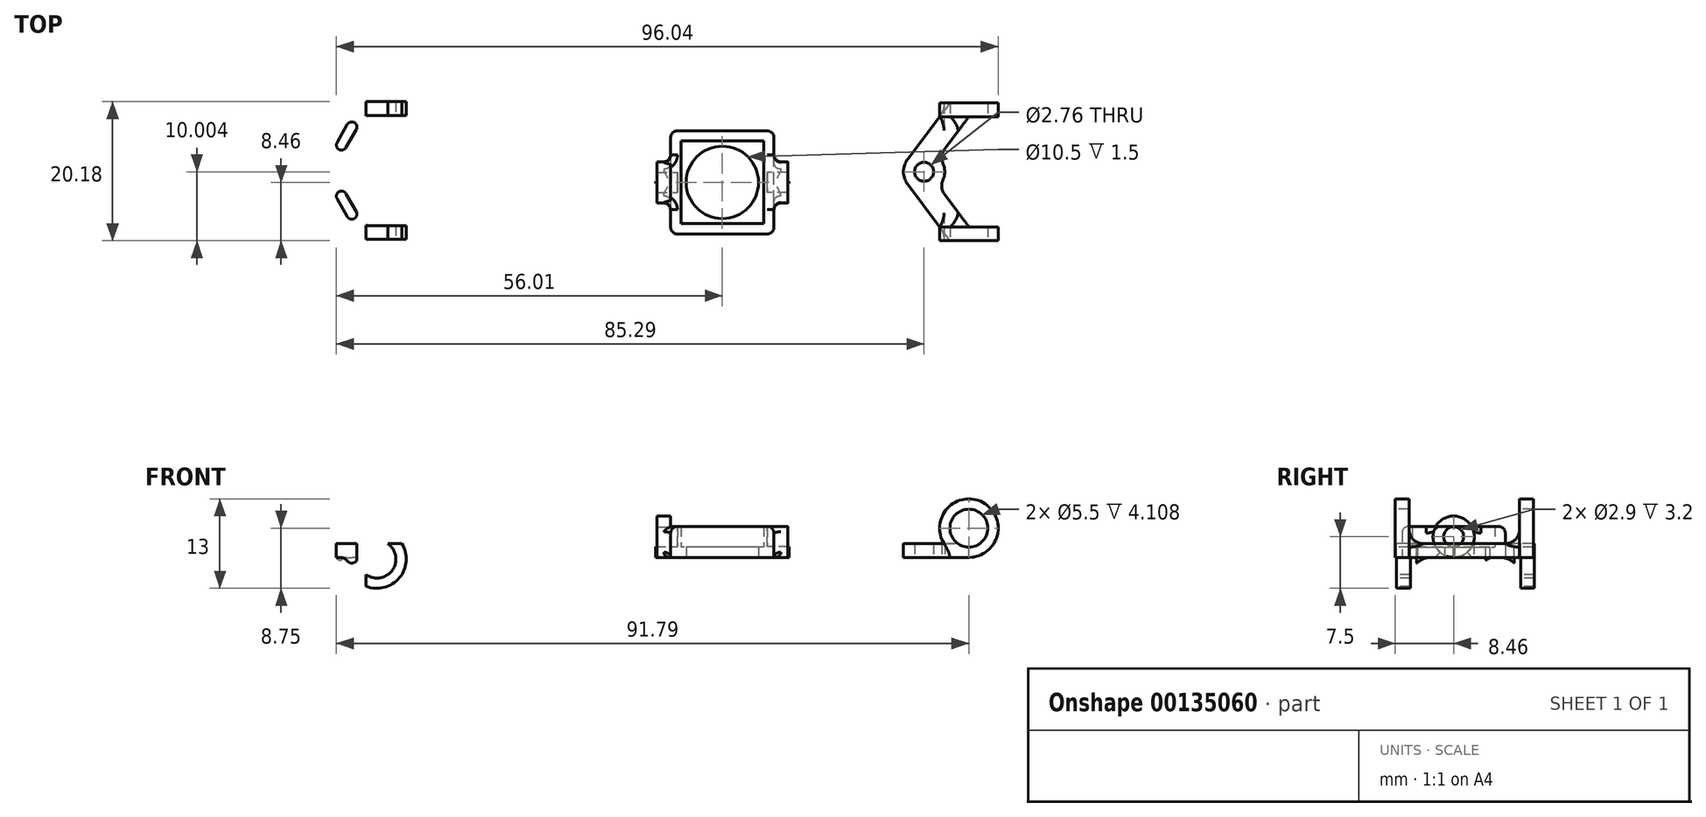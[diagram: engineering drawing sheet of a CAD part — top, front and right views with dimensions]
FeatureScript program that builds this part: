
annotation { "Feature Type Name" : "Feature", "Feature Type Description" : "" }
export const myFeature = defineFeature(function(context is Context, id is Id, definition is map)
    precondition{}
    {
        {
            var Q0;
            Q0=qCreatedBy(makeId("Top.planeOp"),FACE);
            var sketch = newSketch(context, id + "F0", { "sketchPlane" : qUnion([Q0])});
            skLineSegment(sketch, "E0.bottom", {"start": v(6, -6) * mm, "end": v(-6, -6) * mm});
            skLineSegment(sketch, "E0.top", {"start": v(6, 6) * mm, "end": v(-6, 6) * mm});
            skLineSegment(sketch, "E0.left", {"start": v(6, -6) * mm, "end": v(6, 6) * mm});
            skLineSegment(sketch, "E0.right", {"start": v(-6, -6) * mm, "end": v(-6, 6) * mm});
            skPoint(sketch, "E0.middle", {"position": v(0, 0) * mm});
            skLineSegment(sketch, "E1.bottom", {"start": v(7.5, -7.5) * mm, "end": v(-7.5, -7.5) * mm});
            skLineSegment(sketch, "E1.top", {"start": v(7.5, 7.5) * mm, "end": v(-7.5, 7.5) * mm});
            skLineSegment(sketch, "E1.left", {"start": v(7.5, -7.5) * mm, "end": v(7.5, 7.5) * mm});
            skLineSegment(sketch, "E1.right", {"start": v(-7.5, -7.5) * mm, "end": v(-7.5, 7.5) * mm});
            skCircle(sketch, "E2", {"center": v(0, 0) * mm, "radius": 5.25 * mm});
            skSolve(sketch);
        }
        {
            var Q0;
            Q0=makeQuery(id+"F0.imprint","IMPRINT",FACE,{"disambiguationData":[TD([[makeQuery(id+"F0.imprint","IMPRINT",EDGE,{"derivedFrom":sQuery(id+"F0.wireOp",EDGE,"E0.bottom")}),1.0]])]});
            extrude(context, id + "F1", {"entities" : qUnion([Q0]), "depth" : (3 + 1.5) * mm});
        }
        {
            var Q0;
            Q0=makeQuery(id+"F0.imprint","IMPRINT",FACE,{"disambiguationData":[TD([[makeQuery(id+"F0.imprint","IMPRINT",EDGE,{"derivedFrom":sQuery(id+"F0.wireOp",EDGE,"E0.bottom")}),-1.0]])]});
            extrude(context, id + "F2", {"entities" : qUnion([Q0]), "operationType" : NewBodyOperationType.ADD, "depth" : 1.5 * mm});
        }
        {
            var Q0;
            Q0=makeQuery(id+"F1.opExtrude","SWEPT_FACE",FACE,{"disambiguationData":[OSD([sQuery(id+"F0.wireOp",EDGE,"E1.right")])]});
            var sketch = newSketch(context, id + "F3", { "sketchPlane" : qUnion([Q0])});
            skLineSegment(sketch, "E3", {"start": v(0, 0) * mm, "end": v(0, 3) * mm, "construction": true});
            skPoint(sketch, "E3.endSnap0", {"position": v(0, 0) * mm});
            skCircle(sketch, "E4", {"center": v(0, 3) * mm, "radius": 3 * mm});
            skCircle(sketch, "E5", {"center": v(0, 3) * mm, "radius": 1.45 * mm});
            skSolve(sketch);
        }
        {
            var Q0;
            {var subQ0=sQuery(id+"F3.wireOp",EDGE,"E4");var subQ1=makeQuery(id+"F1.opExtrude","CAP_EDGE",EDGE,{"disambiguationData":[OSD([sQuery(id+"F0.wireOp",EDGE,"E1.right")])],"isStart":false});var subQ2=makeQuery(id+"F3.imprint","INTERSECT",VERTEX,{"disambiguationData":[OD(0.0)],"derivedFrom":[subQ1,subQ0]});Q0=makeQuery(id+"F3.imprint","IMPRINT",FACE,{"disambiguationData":[TD([[makeQuery(id+"F3.imprint","IMPRINT",EDGE,{"disambiguationData":[TD([[subQ2,1.0]])],"derivedFrom":subQ0}),1.0]])]});}
            var Q1;
            Q1=makeQuery(id+"F3.imprint","IMPRINT",FACE,{"disambiguationData":[TD([[makeQuery(id+"F3.imprint","IMPRINT",EDGE,{"derivedFrom":sQuery(id+"F3.wireOp",EDGE,"E5")}),-1.0]])]});
            extrude(context, id + "F4", {"entities" : qUnion([Q0, Q1]), "operationType" : NewBodyOperationType.ADD, "depth" : 2 * mm});
        }
        {
            var Q0;
            Q0=makeQuery(id+"F1.opExtrude","SWEPT_FACE",FACE,{"disambiguationData":[OSD([sQuery(id+"F0.wireOp",EDGE,"E1.left")])]});
            var sketch = newSketch(context, id + "F5", { "sketchPlane" : qUnion([Q0])});
            skLineSegment(sketch, "E6", {"start": v(0, 0) * mm, "end": v(0, 3) * mm, "construction": true});
            skPoint(sketch, "E6.endSnap0", {"position": v(0, 0) * mm});
            skCircle(sketch, "E7", {"center": v(0, 3) * mm, "radius": 3 * mm});
            skCircle(sketch, "E8", {"center": v(0, 3) * mm, "radius": 1.45 * mm});
            skSolve(sketch);
        }
        {
            var Q0;
            {var subQ0=sQuery(id+"F5.wireOp",EDGE,"E7");var subQ1=makeQuery(id+"F1.opExtrude","CAP_EDGE",EDGE,{"disambiguationData":[OSD([sQuery(id+"F0.wireOp",EDGE,"E1.left")])],"isStart":false});var subQ2=makeQuery(id+"F5.imprint","INTERSECT",VERTEX,{"disambiguationData":[OD(0.0)],"derivedFrom":[subQ1,subQ0]});Q0=makeQuery(id+"F5.imprint","IMPRINT",FACE,{"disambiguationData":[TD([[makeQuery(id+"F5.imprint","IMPRINT",EDGE,{"disambiguationData":[TD([[subQ2,1.0]])],"derivedFrom":subQ0}),1.0]])]});}
            var Q1;
            Q1=makeQuery(id+"F5.imprint","IMPRINT",FACE,{"disambiguationData":[TD([[makeQuery(id+"F5.imprint","IMPRINT",EDGE,{"derivedFrom":sQuery(id+"F5.wireOp",EDGE,"E8")}),-1.0]])]});
            extrude(context, id + "F6", {"entities" : qUnion([Q0, Q1]), "operationType" : NewBodyOperationType.ADD, "depth" : 2 * mm});
        }
        {
            var Q0;
            {var subQ0=sQuery(id+"F3.wireOp",EDGE,"E4");Q0=makeQuery(id+"F4.boolean.opBoolean","SPLIT",EDGE,{"disambiguationData":[topologyDisambiguationEdgeConnected([makeQuery(id+"F1.opExtrude","SWEPT_FACE",FACE,{"disambiguationData":[OSD([sQuery(id+"F0.wireOp",EDGE,"E1.right")])]}),makeQuery(id+"F4.opExtrude","SWEPT_FACE",FACE,{"disambiguationData":[OSD([subQ0])]})]),OD(0.0)],"derivedFrom":makeQuery(id+"F4.opExtrude","CAP_EDGE",EDGE,{"disambiguationData":[OSD([subQ0])],"isStart":true})});}
            var Q1;
            {var subQ0=sQuery(id+"F3.wireOp",EDGE,"E4");Q1=makeQuery(id+"F4.boolean.opBoolean","SPLIT",EDGE,{"disambiguationData":[topologyDisambiguationEdgeConnected([makeQuery(id+"F1.opExtrude","SWEPT_FACE",FACE,{"disambiguationData":[OSD([sQuery(id+"F0.wireOp",EDGE,"E1.right")])]}),makeQuery(id+"F4.opExtrude","SWEPT_FACE",FACE,{"disambiguationData":[OSD([subQ0])]})]),OD(1.0)],"derivedFrom":makeQuery(id+"F4.opExtrude","CAP_EDGE",EDGE,{"disambiguationData":[OSD([subQ0])],"isStart":true})});}
            var Q2;
            {var subQ0=sQuery(id+"F5.wireOp",EDGE,"E7");Q2=makeQuery(id+"F6.boolean.opBoolean","SPLIT",EDGE,{"disambiguationData":[topologyDisambiguationEdgeConnected([makeQuery(id+"F1.opExtrude","SWEPT_FACE",FACE,{"disambiguationData":[OSD([sQuery(id+"F0.wireOp",EDGE,"E1.left")])]}),makeQuery(id+"F6.opExtrude","SWEPT_FACE",FACE,{"disambiguationData":[OSD([subQ0])]})]),OD(0.0)],"derivedFrom":makeQuery(id+"F6.opExtrude","CAP_EDGE",EDGE,{"disambiguationData":[OSD([subQ0])],"isStart":true})});}
            var Q3;
            {var subQ0=sQuery(id+"F5.wireOp",EDGE,"E7");Q3=makeQuery(id+"F6.boolean.opBoolean","SPLIT",EDGE,{"disambiguationData":[topologyDisambiguationEdgeConnected([makeQuery(id+"F1.opExtrude","SWEPT_FACE",FACE,{"disambiguationData":[OSD([sQuery(id+"F0.wireOp",EDGE,"E1.left")])]}),makeQuery(id+"F6.opExtrude","SWEPT_FACE",FACE,{"disambiguationData":[OSD([subQ0])]})]),OD(1.0)],"derivedFrom":makeQuery(id+"F6.opExtrude","CAP_EDGE",EDGE,{"disambiguationData":[OSD([subQ0])],"isStart":true})});}
            fillet(context, id + "F7", {"entities" : qUnion([Q0, Q1, Q2, Q3]), "radius" : 1 * mm, "tangentPropagation" : true, "allowEdgeOverflow" : false});
        }
        {
            var Q0;
            {var subQ0=sQuery(id+"F0.wireOp",EDGE,"E1.right");Q0=makeQuery(id+"F4.boolean.opBoolean","SPLIT",EDGE,{"disambiguationData":[topologyDisambiguationEdgeConnected([makeQuery(id+"F1.opExtrude","CAP_FACE",FACE,{"disambiguationData":[OSD([sQuery(id+"F0.wireOp",EDGE,"E0.bottom"),sQuery(id+"F0.wireOp",EDGE,"E0.top"),sQuery(id+"F0.wireOp",EDGE,"E0.left"),sQuery(id+"F0.wireOp",EDGE,"E0.right"),sQuery(id+"F0.wireOp",EDGE,"E1.bottom"),sQuery(id+"F0.wireOp",EDGE,"E1.top"),sQuery(id+"F0.wireOp",EDGE,"E1.left"),subQ0])],"isStart":false}),makeQuery(id+"F4.opExtrude","CAP_FACE",FACE,{"disambiguationData":[OSD([sQuery(id+"F3.wireOp",EDGE,"E4"),sQuery(id+"F3.wireOp",EDGE,"E5")])],"isStart":true})])],"derivedFrom":makeQuery(id+"F1.opExtrude","CAP_EDGE",EDGE,{"disambiguationData":[OSD([subQ0])],"isStart":false})});}
            var Q1;
            {var subQ0=sQuery(id+"F0.wireOp",EDGE,"E1.left");Q1=makeQuery(id+"F6.boolean.opBoolean","SPLIT",EDGE,{"disambiguationData":[topologyDisambiguationEdgeConnected([makeQuery(id+"F1.opExtrude","CAP_FACE",FACE,{"disambiguationData":[OSD([sQuery(id+"F0.wireOp",EDGE,"E0.bottom"),sQuery(id+"F0.wireOp",EDGE,"E0.top"),sQuery(id+"F0.wireOp",EDGE,"E0.left"),sQuery(id+"F0.wireOp",EDGE,"E0.right"),sQuery(id+"F0.wireOp",EDGE,"E1.bottom"),sQuery(id+"F0.wireOp",EDGE,"E1.top"),subQ0,sQuery(id+"F0.wireOp",EDGE,"E1.right")])],"isStart":false}),makeQuery(id+"F6.opExtrude","CAP_FACE",FACE,{"disambiguationData":[OSD([sQuery(id+"F5.wireOp",EDGE,"E7"),sQuery(id+"F5.wireOp",EDGE,"E8")])],"isStart":true})])],"derivedFrom":makeQuery(id+"F1.opExtrude","CAP_EDGE",EDGE,{"disambiguationData":[OSD([subQ0])],"isStart":false})});}
            var Q2;
            {var subQ0=sQuery(id+"F3.wireOp",EDGE,"E4");var subQ1=sQuery(id+"F0.wireOp",EDGE,"E1.right");Q2=makeQuery(id+"F7.opFillet","TWEAK_EDGE",EDGE,{"derivedFrom":[makeQuery(id+"F4.boolean.opBoolean","TWEAK_VERTEX",VERTEX,{"disambiguationData":[OD(0.0)],"derivedFrom":[makeQuery(id+"F1.opExtrude","CAP_FACE",FACE,{"disambiguationData":[OSD([sQuery(id+"F0.wireOp",EDGE,"E0.bottom"),sQuery(id+"F0.wireOp",EDGE,"E0.top"),sQuery(id+"F0.wireOp",EDGE,"E0.left"),sQuery(id+"F0.wireOp",EDGE,"E0.right"),sQuery(id+"F0.wireOp",EDGE,"E1.bottom"),sQuery(id+"F0.wireOp",EDGE,"E1.top"),sQuery(id+"F0.wireOp",EDGE,"E1.left"),subQ1])],"isStart":false}),makeQuery(id+"F1.opExtrude","SWEPT_FACE",FACE,{"disambiguationData":[OSD([subQ1])]}),makeQuery(id+"F4.opExtrude","SWEPT_FACE",FACE,{"disambiguationData":[OSD([subQ0])]}),makeQuery(id+"F4.opExtrude","CAP_FACE",FACE,{"disambiguationData":[OSD([subQ0,sQuery(id+"F3.wireOp",EDGE,"E5")])],"isStart":true})]})]});}
            var Q3;
            {var subQ0=sQuery(id+"F3.wireOp",EDGE,"E4");var subQ1=sQuery(id+"F0.wireOp",EDGE,"E1.right");Q3=makeQuery(id+"F7.opFillet","TWEAK_EDGE",EDGE,{"derivedFrom":[makeQuery(id+"F4.boolean.opBoolean","TWEAK_VERTEX",VERTEX,{"disambiguationData":[OD(1.0)],"derivedFrom":[makeQuery(id+"F1.opExtrude","CAP_FACE",FACE,{"disambiguationData":[OSD([sQuery(id+"F0.wireOp",EDGE,"E0.bottom"),sQuery(id+"F0.wireOp",EDGE,"E0.top"),sQuery(id+"F0.wireOp",EDGE,"E0.left"),sQuery(id+"F0.wireOp",EDGE,"E0.right"),sQuery(id+"F0.wireOp",EDGE,"E1.bottom"),sQuery(id+"F0.wireOp",EDGE,"E1.top"),sQuery(id+"F0.wireOp",EDGE,"E1.left"),subQ1])],"isStart":false}),makeQuery(id+"F1.opExtrude","SWEPT_FACE",FACE,{"disambiguationData":[OSD([subQ1])]}),makeQuery(id+"F4.opExtrude","SWEPT_FACE",FACE,{"disambiguationData":[OSD([subQ0])]}),makeQuery(id+"F4.opExtrude","CAP_FACE",FACE,{"disambiguationData":[OSD([subQ0,sQuery(id+"F3.wireOp",EDGE,"E5")])],"isStart":true})]})]});}
            var Q4;
            {var subQ0=sQuery(id+"F5.wireOp",EDGE,"E7");var subQ1=sQuery(id+"F0.wireOp",EDGE,"E1.left");Q4=makeQuery(id+"F7.opFillet","TWEAK_EDGE",EDGE,{"derivedFrom":[makeQuery(id+"F6.boolean.opBoolean","TWEAK_VERTEX",VERTEX,{"disambiguationData":[OD(1.0)],"derivedFrom":[makeQuery(id+"F1.opExtrude","CAP_FACE",FACE,{"disambiguationData":[OSD([sQuery(id+"F0.wireOp",EDGE,"E0.bottom"),sQuery(id+"F0.wireOp",EDGE,"E0.top"),sQuery(id+"F0.wireOp",EDGE,"E0.left"),sQuery(id+"F0.wireOp",EDGE,"E0.right"),sQuery(id+"F0.wireOp",EDGE,"E1.bottom"),sQuery(id+"F0.wireOp",EDGE,"E1.top"),subQ1,sQuery(id+"F0.wireOp",EDGE,"E1.right")])],"isStart":false}),makeQuery(id+"F1.opExtrude","SWEPT_FACE",FACE,{"disambiguationData":[OSD([subQ1])]}),makeQuery(id+"F6.opExtrude","SWEPT_FACE",FACE,{"disambiguationData":[OSD([subQ0])]}),makeQuery(id+"F6.opExtrude","CAP_FACE",FACE,{"disambiguationData":[OSD([subQ0,sQuery(id+"F5.wireOp",EDGE,"E8")])],"isStart":true})]})]});}
            var Q5;
            {var subQ0=sQuery(id+"F5.wireOp",EDGE,"E7");var subQ1=sQuery(id+"F0.wireOp",EDGE,"E1.left");Q5=makeQuery(id+"F7.opFillet","TWEAK_EDGE",EDGE,{"derivedFrom":[makeQuery(id+"F6.boolean.opBoolean","TWEAK_VERTEX",VERTEX,{"disambiguationData":[OD(0.0)],"derivedFrom":[makeQuery(id+"F1.opExtrude","CAP_FACE",FACE,{"disambiguationData":[OSD([sQuery(id+"F0.wireOp",EDGE,"E0.bottom"),sQuery(id+"F0.wireOp",EDGE,"E0.top"),sQuery(id+"F0.wireOp",EDGE,"E0.left"),sQuery(id+"F0.wireOp",EDGE,"E0.right"),sQuery(id+"F0.wireOp",EDGE,"E1.bottom"),sQuery(id+"F0.wireOp",EDGE,"E1.top"),subQ1,sQuery(id+"F0.wireOp",EDGE,"E1.right")])],"isStart":false}),makeQuery(id+"F1.opExtrude","SWEPT_FACE",FACE,{"disambiguationData":[OSD([subQ1])]}),makeQuery(id+"F6.opExtrude","SWEPT_FACE",FACE,{"disambiguationData":[OSD([subQ0])]}),makeQuery(id+"F6.opExtrude","CAP_FACE",FACE,{"disambiguationData":[OSD([subQ0,sQuery(id+"F5.wireOp",EDGE,"E8")])],"isStart":true})]})]});}
            fillet(context, id + "F8", {"entities" : qUnion([Q0, Q1, Q2, Q3, Q4, Q5]), "radius" : 1 * mm, "tangentPropagation" : true, "allowEdgeOverflow" : false});
        }
        {
            var Q0;
            Q0=makeQuery(id+"F6.boolean.opBoolean","SPLIT",FACE,{"disambiguationData":[TD([makeQuery(id+"F6.opExtrude","SWEPT_FACE",FACE,{"disambiguationData":[OSD([sQuery(id+"F5.wireOp",EDGE,"E8")])]})])],"derivedFrom":makeQuery(id+"F1.opExtrude","SWEPT_FACE",FACE,{"disambiguationData":[OSD([sQuery(id+"F0.wireOp",EDGE,"E1.left")])]})});
            extrude(context, id + "F9", {"entities" : qUnion([Q0]), "operationType" : NewBodyOperationType.REMOVE, "oppositeDirection" : true, "depth" : 1 * mm});
        }
        {
            var Q0;
            Q0=makeQuery(id+"F4.boolean.opBoolean","SPLIT",FACE,{"disambiguationData":[TD([makeQuery(id+"F4.opExtrude","SWEPT_FACE",FACE,{"disambiguationData":[OSD([sQuery(id+"F3.wireOp",EDGE,"E5")])]})])],"derivedFrom":makeQuery(id+"F1.opExtrude","SWEPT_FACE",FACE,{"disambiguationData":[OSD([sQuery(id+"F0.wireOp",EDGE,"E1.right")])]})});
            extrude(context, id + "F10", {"entities" : qUnion([Q0]), "operationType" : NewBodyOperationType.REMOVE, "oppositeDirection" : true, "depth" : 1 * mm});
        }
        {
            var Q0;
            Q0=qCreatedBy(makeId("Top.planeOp"),FACE);
            var sketch = newSketch(context, id + "F11", { "sketchPlane" : qUnion([Q0])});
            skLineSegment(sketch, "E9", {"start": v(35.78, 11.54) * mm, "end": v(35.78, -8.46) * mm, "construction": true});
            skLineSegment(sketch, "E10", {"start": v(33.28, 1.54) * mm, "end": v(29.28, 1.54) * mm, "construction": true});
            skCircle(sketch, "E11", {"center": v(29.28, 1.54) * mm, "radius": 1.38 * mm});
            skCircle(sketch, "E12", {"center": v(29.28, 1.54) * mm, "radius": 3 * mm});
            skLineSegment(sketch, "E13", {"start": v(35.78, 1.54) * mm, "end": v(33.28, 1.54) * mm, "construction": true});
            skLineSegment(sketch, "E14.bottom", {"start": v(35.78, 11.54) * mm, "end": v(33.03, 11.54) * mm});
            skLineSegment(sketch, "E14.top", {"start": v(35.78, 9.54) * mm, "end": v(33.03, 9.54) * mm});
            skLineSegment(sketch, "E14.left", {"start": v(35.78, 11.54) * mm, "end": v(35.78, 9.54) * mm});
            skLineSegment(sketch, "E14.right", {"start": v(33.03, 11.54) * mm, "end": v(33.03, 9.54) * mm});
            skLineSegment(sketch, "E15.bottom", {"start": v(35.78, -8.46) * mm, "end": v(33.03, -8.46) * mm});
            skLineSegment(sketch, "E15.top", {"start": v(35.78, -6.46) * mm, "end": v(33.03, -6.46) * mm});
            skLineSegment(sketch, "E15.left", {"start": v(35.78, -8.46) * mm, "end": v(35.78, -6.46) * mm});
            skLineSegment(sketch, "E15.right", {"start": v(33.03, -8.46) * mm, "end": v(33.03, -6.46) * mm});
            skLineSegment(sketch, "E16", {"start": v(33.03, 11.54) * mm, "end": v(26.88, 3.34) * mm});
            skLineSegment(sketch, "E17", {"start": v(33.03, -8.46) * mm, "end": v(26.88, -0.26) * mm});
            skLineSegment(sketch, "E18", {"start": v(35.78, 9.54) * mm, "end": v(31.38, 3.68) * mm});
            skLineSegment(sketch, "E19", {"start": v(35.78, -6.46) * mm, "end": v(31.38, -0.6) * mm});
            skSolve(sketch);
        }
        {
            var Q0;
            Q0=makeQuery(id+"F11.imprint","IMPRINT",FACE,{"disambiguationData":[TD([[makeQuery(id+"F11.imprint","IMPRINT",EDGE,{"derivedFrom":sQuery(id+"F11.wireOp",EDGE,"E15.top")}),-1.0]])]});
            var Q1;
            Q1=makeQuery(id+"F11.imprint","IMPRINT",FACE,{"disambiguationData":[TD([[makeQuery(id+"F11.imprint","IMPRINT",EDGE,{"derivedFrom":sQuery(id+"F11.wireOp",EDGE,"E15.bottom")}),-1.0]])]});
            var Q2;
            Q2=makeQuery(id+"F11.imprint","IMPRINT",FACE,{"disambiguationData":[TD([[makeQuery(id+"F11.imprint","IMPRINT",EDGE,{"derivedFrom":sQuery(id+"F11.wireOp",EDGE,"E11")}),-1.0]])]});
            var Q3;
            Q3=makeQuery(id+"F11.imprint","IMPRINT",FACE,{"disambiguationData":[TD([[makeQuery(id+"F11.imprint","IMPRINT",EDGE,{"derivedFrom":sQuery(id+"F11.wireOp",EDGE,"E14.top")}),1.0]])]});
            var Q4;
            Q4=makeQuery(id+"F11.imprint","IMPRINT",FACE,{"disambiguationData":[TD([[makeQuery(id+"F11.imprint","IMPRINT",EDGE,{"derivedFrom":sQuery(id+"F11.wireOp",EDGE,"E14.bottom")}),1.0]])]});
            extrude(context, id + "F12", {"entities" : qUnion([Q0, Q1, Q2, Q3, Q4]), "depth" : 2 * mm});
        }
        {
            var Q0;
            Q0=makeQuery(id+"F12.opExtrude","SWEPT_FACE",FACE,{"disambiguationData":[OSD([sQuery(id+"F11.wireOp",EDGE,"E15.bottom")])]});
            var sketch = newSketch(context, id + "F13", { "sketchPlane" : qUnion([Q0])});
            skLineSegment(sketch, "E20", {"start": v(35.78, 0) * mm, "end": v(35.78, 4.25) * mm, "construction": true});
            skCircle(sketch, "E21", {"center": v(35.78, 4.25) * mm, "radius": 4.25 * mm});
            skCircle(sketch, "E22", {"center": v(35.78, 4.25) * mm, "radius": 2.75 * mm});
            skSolve(sketch);
        }
        {
            var Q0;
            {var subQ0=sQuery(id+"F11.wireOp",EDGE,"E15.bottom");var subQ1=makeQuery(id+"F12.opExtrude","CAP_EDGE",EDGE,{"disambiguationData":[OSD([subQ0])],"isStart":false});var subQ8=sQuery(id+"F13.wireOp",EDGE,"E22");var subQ10=makeQuery(id+"F13.imprint","INTERSECT",VERTEX,{"derivedFrom":[subQ1,subQ8]});Q0=makeQuery(id+"F13.imprint","IMPRINT",FACE,{"disambiguationData":[TD([[makeQuery(id+"F13.imprint","IMPRINT",EDGE,{"disambiguationData":[TD([[subQ10,1.0]])],"derivedFrom":subQ8}),-1.0]])]});}
            var Q1;
            {var subQ1=sQuery(id+"F11.wireOp",EDGE,"E15.bottom");var subQ4=sQuery(id+"F13.wireOp",EDGE,"E22");var subQ6=makeQuery(id+"F12.opExtrude","CAP_EDGE",EDGE,{"disambiguationData":[OSD([subQ1])],"isStart":false});var subQ7=makeQuery(id+"F13.imprint","INTERSECT",VERTEX,{"derivedFrom":[subQ6,subQ4]});Q1=makeQuery(id+"F13.imprint","IMPRINT",FACE,{"disambiguationData":[TD([[makeQuery(id+"F13.imprint","IMPRINT",EDGE,{"disambiguationData":[TD([[subQ7,-1.0]])],"derivedFrom":subQ4}),-1.0]])]});}
            extrude(context, id + "F14", {"entities" : qUnion([Q0, Q1]), "operationType" : NewBodyOperationType.ADD, "oppositeDirection" : true, "depth" : 2 * mm});
        }
        {
            var Q0;
            {var subQ0=sQuery(id+"F13.wireOp",EDGE,"E22");var subQ1=sQuery(id+"F11.wireOp",EDGE,"E15.bottom");var subQ4=makeQuery(id+"F12.opExtrude","CAP_EDGE",EDGE,{"disambiguationData":[OSD([subQ1])],"isStart":false});var subQ5=makeQuery(id+"F13.imprint","INTERSECT",VERTEX,{"derivedFrom":[subQ4,subQ0]});Q0=makeQuery(id+"F13.imprint","IMPRINT",FACE,{"disambiguationData":[TD([[makeQuery(id+"F13.imprint","IMPRINT",EDGE,{"disambiguationData":[TD([[subQ5,-1.0]])],"derivedFrom":subQ0}),1.0]])]});}
            extrude(context, id + "F15", {"entities" : qUnion([Q0]), "operationType" : NewBodyOperationType.REMOVE, "oppositeDirection" : true, "depth" : 25 * mm});
        }
        {
            var Q0;
            {var subQ0=sQuery(id+"F11.wireOp",EDGE,"E15.bottom");var subQ1=makeQuery(id+"F12.opExtrude","CAP_EDGE",EDGE,{"disambiguationData":[OSD([subQ0])],"isStart":false});var subQ8=sQuery(id+"F13.wireOp",EDGE,"E22");var subQ10=makeQuery(id+"F13.imprint","INTERSECT",VERTEX,{"derivedFrom":[subQ1,subQ8]});Q0=makeQuery(id+"F13.imprint","IMPRINT",FACE,{"disambiguationData":[TD([[makeQuery(id+"F13.imprint","IMPRINT",EDGE,{"disambiguationData":[TD([[subQ10,1.0]])],"derivedFrom":subQ8}),-1.0]])]});}
            var Q1;
            {var subQ1=sQuery(id+"F11.wireOp",EDGE,"E15.bottom");var subQ4=sQuery(id+"F13.wireOp",EDGE,"E22");var subQ6=makeQuery(id+"F12.opExtrude","CAP_EDGE",EDGE,{"disambiguationData":[OSD([subQ1])],"isStart":false});var subQ7=makeQuery(id+"F13.imprint","INTERSECT",VERTEX,{"derivedFrom":[subQ6,subQ4]});Q1=makeQuery(id+"F13.imprint","IMPRINT",FACE,{"disambiguationData":[TD([[makeQuery(id+"F13.imprint","IMPRINT",EDGE,{"disambiguationData":[TD([[subQ7,-1.0]])],"derivedFrom":subQ4}),-1.0]])]});}
            var Q2;
            Q2=makeQuery(id+"F12.opExtrude","SWEPT_FACE",FACE,{"disambiguationData":[OSD([sQuery(id+"F11.wireOp",EDGE,"E14.bottom")])]});
            extrude(context, id + "F16", {"entities" : qUnion([Q0, Q1]), "operationType" : NewBodyOperationType.ADD, "endBound" : BoundingType.UP_TO_SURFACE, "oppositeDirection" : true, "endBoundEntityFace" : qUnion([Q2]), "depth" : 25 * mm, "hasSecondDirection" : true, "secondDirectionOppositeDirection" : true, "secondDirectionDepth" : 18 * mm});
        }
        {
            var Q0;
            Q0=makeQuery(id+"F16.boolean.opBoolean","INTERSECT",EDGE,{"derivedFrom":[makeQuery(id+"F12.opExtrude","CAP_FACE",FACE,{"disambiguationData":[OSD([sQuery(id+"F11.wireOp",EDGE,"E11"),sQuery(id+"F11.wireOp",EDGE,"E12"),sQuery(id+"F11.wireOp",EDGE,"E14.bottom"),sQuery(id+"F11.wireOp",EDGE,"E14.left"),sQuery(id+"F11.wireOp",EDGE,"E15.bottom"),sQuery(id+"F11.wireOp",EDGE,"E15.left"),sQuery(id+"F11.wireOp",EDGE,"E16"),sQuery(id+"F11.wireOp",EDGE,"E17"),sQuery(id+"F11.wireOp",EDGE,"E18"),sQuery(id+"F11.wireOp",EDGE,"E19")])],"isStart":false}),makeQuery(id+"F16.opExtrude","CAP_FACE",FACE,{"disambiguationData":[OSD([sQuery(id+"F13.wireOp",EDGE,"E21"),sQuery(id+"F13.wireOp",EDGE,"E22")])],"isStart":true})]});
            var Q1;
            Q1=makeQuery(id+"F14.boolean.opBoolean","INTERSECT",EDGE,{"derivedFrom":[makeQuery(id+"F12.opExtrude","CAP_FACE",FACE,{"disambiguationData":[OSD([sQuery(id+"F11.wireOp",EDGE,"E11"),sQuery(id+"F11.wireOp",EDGE,"E12"),sQuery(id+"F11.wireOp",EDGE,"E14.bottom"),sQuery(id+"F11.wireOp",EDGE,"E14.left"),sQuery(id+"F11.wireOp",EDGE,"E15.bottom"),sQuery(id+"F11.wireOp",EDGE,"E15.left"),sQuery(id+"F11.wireOp",EDGE,"E16"),sQuery(id+"F11.wireOp",EDGE,"E17"),sQuery(id+"F11.wireOp",EDGE,"E18"),sQuery(id+"F11.wireOp",EDGE,"E19")])],"isStart":false}),makeQuery(id+"F14.opExtrude","CAP_FACE",FACE,{"disambiguationData":[OSD([sQuery(id+"F13.wireOp",EDGE,"E21"),sQuery(id+"F13.wireOp",EDGE,"E22")])],"isStart":false})]});
            var Q2;
            {var subQ0=sQuery(id+"F13.wireOp",EDGE,"E21");var subQ1=sQuery(id+"F11.wireOp",EDGE,"E19");var subQ2=sQuery(id+"F11.wireOp",EDGE,"E15.left");Q2=makeQuery(id+"F14.boolean.opBoolean","SPLIT",EDGE,{"disambiguationData":[TD([makeQuery(id+"F14.opExtrude","SWEPT_FACE",FACE,{"disambiguationData":[OSD([subQ0])]})])],"derivedFrom":makeQuery(id+"F12.opExtrude","SWEPT_EDGE",EDGE,{"disambiguationData":[OSD([sQuery(id+"F11.wireOp",EDGE,"E15.top"),subQ2,subQ1])]})});}
            var Q3;
            Q3=makeQuery(id+"F12.opExtrude","SWEPT_EDGE",EDGE,{"disambiguationData":[OSD([sQuery(id+"F11.wireOp",EDGE,"E14.top"),sQuery(id+"F11.wireOp",EDGE,"E14.left"),sQuery(id+"F11.wireOp",EDGE,"E18")])]});
            var Q4;
            Q4=makeQuery(id+"F12.opExtrude","SWEPT_EDGE",EDGE,{"disambiguationData":[OSD([sQuery(id+"F11.wireOp",EDGE,"E12"),sQuery(id+"F11.wireOp",EDGE,"E18")])]});
            var Q5;
            Q5=makeQuery(id+"F12.opExtrude","SWEPT_EDGE",EDGE,{"disambiguationData":[OSD([sQuery(id+"F11.wireOp",EDGE,"E12"),sQuery(id+"F11.wireOp",EDGE,"E19")])]});
            var Q6;
            Q6=makeQuery(id+"F14.boolean.opBoolean","INTERSECT",EDGE,{"derivedFrom":[makeQuery(id+"F12.opExtrude","SWEPT_FACE",FACE,{"disambiguationData":[OSD([sQuery(id+"F11.wireOp",EDGE,"E17")])]}),makeQuery(id+"F14.opExtrude","SWEPT_FACE",FACE,{"disambiguationData":[OSD([sQuery(id+"F13.wireOp",EDGE,"E21")])]})]});
            var Q7;
            Q7=makeQuery(id+"F16.boolean.opBoolean","INTERSECT",EDGE,{"derivedFrom":[makeQuery(id+"F12.opExtrude","SWEPT_FACE",FACE,{"disambiguationData":[OSD([sQuery(id+"F11.wireOp",EDGE,"E16")])]}),makeQuery(id+"F16.opExtrude","SWEPT_FACE",FACE,{"disambiguationData":[OSD([sQuery(id+"F13.wireOp",EDGE,"E21")])]})]});
            fillet(context, id + "F17", {"entities" : qUnion([Q0, Q1, Q2, Q3, Q4, Q5, Q6, Q7]), "radius" : 2 * mm, "tangentPropagation" : true, "allowEdgeOverflow" : false});
        }
        {
            var Q0;
            Q0=qCreatedBy(makeId("Top.planeOp"),FACE);
            var sketch = newSketch(context, id + "F18", { "sketchPlane" : qUnion([Q0])});
            skLineSegment(sketch, "E23", {"start": v(-50.12, 11.72) * mm, "end": v(-50.12, -8.28) * mm, "construction": true});
            skLineSegment(sketch, "E24", {"start": v(-50.12, 1.72) * mm, "end": v(-52.62, 1.72) * mm, "construction": true});
            skLineSegment(sketch, "E25", {"start": v(-52.62, 1.72) * mm, "end": v(-56.62, 1.72) * mm, "construction": true});
            skCircle(sketch, "E26", {"center": v(-56.62, 1.72) * mm, "radius": 1.45 * mm});
            skCircle(sketch, "E27", {"center": v(-56.62, 1.72) * mm, "radius": 3 * mm});
            skLineSegment(sketch, "E28.bottom", {"start": v(-50.12, 11.72) * mm, "end": v(-54.37, 11.72) * mm});
            skLineSegment(sketch, "E28.top", {"start": v(-50.12, 9.72) * mm, "end": v(-54.37, 9.72) * mm});
            skLineSegment(sketch, "E28.left", {"start": v(-50.12, 11.72) * mm, "end": v(-50.12, 9.72) * mm});
            skLineSegment(sketch, "E28.right", {"start": v(-54.37, 11.72) * mm, "end": v(-54.37, 9.72) * mm});
            skLineSegment(sketch, "E29.bottom", {"start": v(-50.12, -8.28) * mm, "end": v(-54.37, -8.28) * mm});
            skLineSegment(sketch, "E29.top", {"start": v(-50.12, -6.28) * mm, "end": v(-54.37, -6.28) * mm});
            skLineSegment(sketch, "E29.left", {"start": v(-50.12, -8.28) * mm, "end": v(-50.12, -6.28) * mm});
            skLineSegment(sketch, "E29.right", {"start": v(-54.37, -8.28) * mm, "end": v(-54.37, -6.28) * mm});
            skLineSegment(sketch, "E30", {"start": v(-54.37, 11.72) * mm, "end": v(-59.22, 3.2) * mm});
            skLineSegment(sketch, "E31", {"start": v(-54.37, -8.28) * mm, "end": v(-59.22, 0.23) * mm});
            skLineSegment(sketch, "E32", {"start": v(-50.12, -6.28) * mm, "end": v(-53.92, 0.4) * mm});
            skLineSegment(sketch, "E33", {"start": v(-50.12, 9.72) * mm, "end": v(-53.92, 3.04) * mm});
            skSolve(sketch);
        }
        {
            var Q0;
            Q0=makeQuery(id+"F18.imprint","IMPRINT",FACE,{"disambiguationData":[TD([[makeQuery(id+"F18.imprint","IMPRINT",EDGE,{"derivedFrom":sQuery(id+"F18.wireOp",EDGE,"E28.bottom")}),1.0]])]});
            var Q1;
            Q1=makeQuery(id+"F18.imprint","IMPRINT",FACE,{"disambiguationData":[TD([[makeQuery(id+"F18.imprint","IMPRINT",EDGE,{"derivedFrom":sQuery(id+"F18.wireOp",EDGE,"E28.top")}),1.0]])]});
            var Q2;
            Q2=makeQuery(id+"F18.imprint","IMPRINT",FACE,{"disambiguationData":[TD([[makeQuery(id+"F18.imprint","IMPRINT",EDGE,{"derivedFrom":sQuery(id+"F18.wireOp",EDGE,"E26")}),-1.0]])]});
            var Q3;
            Q3=makeQuery(id+"F18.imprint","IMPRINT",FACE,{"disambiguationData":[TD([[makeQuery(id+"F18.imprint","IMPRINT",EDGE,{"derivedFrom":sQuery(id+"F18.wireOp",EDGE,"E29.top")}),-1.0]])]});
            var Q4;
            Q4=makeQuery(id+"F18.imprint","IMPRINT",FACE,{"disambiguationData":[TD([[makeQuery(id+"F18.imprint","IMPRINT",EDGE,{"derivedFrom":sQuery(id+"F18.wireOp",EDGE,"E29.bottom")}),-1.0]])]});
            extrude(context, id + "F19", {"entities" : qUnion([Q0, Q1, Q2, Q3, Q4]), "depth" : 2 * mm});
        }
        {
            var Q0;
            Q0=makeQuery(id+"F19.opExtrude","SWEPT_FACE",FACE,{"disambiguationData":[OSD([sQuery(id+"F18.wireOp",EDGE,"E29.bottom")])]});
            var sketch = newSketch(context, id + "F20", { "sketchPlane" : qUnion([Q0])});
            skLineSegment(sketch, "E34", {"start": v(-50.12, 2) * mm, "end": v(-50.12, -0.25) * mm, "construction": true});
            skPoint(sketch, "E34.endSnap0", {"position": v(-50.12, 1) * mm});
            skCircle(sketch, "E35", {"center": v(-50.12, -0.25) * mm, "radius": 2.75 * mm});
            skCircle(sketch, "E36", {"center": v(-50.12, -0.25) * mm, "radius": 4.25 * mm});
            skLineSegment(sketch, "E37", {"start": v(-54.37, 2) * mm, "end": v(-46.51, 2) * mm});
            skSolve(sketch);
        }
        {
            var Q0;
            {var subQ0=sQuery(id+"F20.wireOp",EDGE,"E37");var subQ1=sQuery(id+"F20.wireOp",EDGE,"E35");var subQ2=makeQuery(id+"F20.imprint","INTERSECT",VERTEX,{"disambiguationData":[OD(0.0)],"derivedFrom":[subQ1,subQ0]});Q0=makeQuery(id+"F20.imprint","IMPRINT",FACE,{"disambiguationData":[TD([[makeQuery(id+"F20.imprint","IMPRINT",EDGE,{"disambiguationData":[TD([[subQ2,-1.0]])],"derivedFrom":subQ1}),-1.0]])]});}
            var Q1;
            {var subQ0=sQuery(id+"F20.wireOp",EDGE,"E37");var subQ1=sQuery(id+"F20.wireOp",EDGE,"E35");var subQ2=makeQuery(id+"F20.imprint","INTERSECT",VERTEX,{"disambiguationData":[OD(1.0)],"derivedFrom":[subQ1,subQ0]});Q1=makeQuery(id+"F20.imprint","IMPRINT",FACE,{"disambiguationData":[TD([[makeQuery(id+"F20.imprint","IMPRINT",EDGE,{"disambiguationData":[TD([[subQ2,1.0]])],"derivedFrom":subQ1}),-1.0]])]});}
            extrude(context, id + "F21", {"entities" : qUnion([Q0, Q1]), "operationType" : NewBodyOperationType.ADD, "oppositeDirection" : true, "depth" : 2 * mm});
        }
        {
            var Q0;
            {var subQ3=sQuery(id+"F18.wireOp",EDGE,"E29.bottom");var subQ6=makeQuery(id+"F19.opExtrude","SWEPT_EDGE",EDGE,{"disambiguationData":[OSD([subQ3,sQuery(id+"F18.wireOp",EDGE,"E29.left")])]});Q0=makeQuery(id+"F20.imprint","IMPRINT",FACE,{"disambiguationData":[TD([[makeQuery(id+"F20.imprint","IMPRINT",EDGE,{"derivedFrom":subQ6}),-1.0]])]});}
            extrude(context, id + "F22", {"entities" : qUnion([Q0]), "operationType" : NewBodyOperationType.REMOVE, "oppositeDirection" : true, "depth" : 25 * mm});
        }
        {
            var Q0;
            {var subQ0=sQuery(id+"F20.wireOp",EDGE,"E37");var subQ1=sQuery(id+"F20.wireOp",EDGE,"E35");var subQ2=makeQuery(id+"F20.imprint","INTERSECT",VERTEX,{"disambiguationData":[OD(0.0)],"derivedFrom":[subQ1,subQ0]});Q0=makeQuery(id+"F20.imprint","IMPRINT",FACE,{"disambiguationData":[TD([[makeQuery(id+"F20.imprint","IMPRINT",EDGE,{"disambiguationData":[TD([[subQ2,-1.0]])],"derivedFrom":subQ1}),-1.0]])]});}
            var Q1;
            {var subQ0=sQuery(id+"F20.wireOp",EDGE,"E37");var subQ1=sQuery(id+"F20.wireOp",EDGE,"E35");var subQ2=makeQuery(id+"F20.imprint","INTERSECT",VERTEX,{"disambiguationData":[OD(1.0)],"derivedFrom":[subQ1,subQ0]});Q1=makeQuery(id+"F20.imprint","IMPRINT",FACE,{"disambiguationData":[TD([[makeQuery(id+"F20.imprint","IMPRINT",EDGE,{"disambiguationData":[TD([[subQ2,1.0]])],"derivedFrom":subQ1}),-1.0]])]});}
            var Q2;
            Q2=makeQuery(id+"F19.opExtrude","SWEPT_FACE",FACE,{"disambiguationData":[OSD([sQuery(id+"F18.wireOp",EDGE,"E28.bottom")])]});
            extrude(context, id + "F23", {"entities" : qUnion([Q0, Q1]), "operationType" : NewBodyOperationType.ADD, "endBound" : BoundingType.UP_TO_SURFACE, "oppositeDirection" : true, "endBoundEntityFace" : qUnion([Q2]), "depth" : 25 * mm, "hasSecondDirection" : true, "secondDirectionOppositeDirection" : true, "secondDirectionDepth" : 18 * mm});
        }
        {
            var Q0;
            Q0=makeQuery(id+"F21.boolean.opBoolean","INTERSECT",EDGE,{"derivedFrom":[makeQuery(id+"F19.opExtrude","CAP_FACE",FACE,{"disambiguationData":[OSD([sQuery(id+"F18.wireOp",EDGE,"E26"),sQuery(id+"F18.wireOp",EDGE,"E27"),sQuery(id+"F18.wireOp",EDGE,"E28.bottom"),sQuery(id+"F18.wireOp",EDGE,"E28.left"),sQuery(id+"F18.wireOp",EDGE,"E29.bottom"),sQuery(id+"F18.wireOp",EDGE,"E29.left"),sQuery(id+"F18.wireOp",EDGE,"E30"),sQuery(id+"F18.wireOp",EDGE,"E31"),sQuery(id+"F18.wireOp",EDGE,"E32"),sQuery(id+"F18.wireOp",EDGE,"E33")])],"isStart":true}),makeQuery(id+"F21.opExtrude","CAP_FACE",FACE,{"disambiguationData":[OSD([sQuery(id+"F20.wireOp",EDGE,"E35"),sQuery(id+"F20.wireOp",EDGE,"E36"),sQuery(id+"F20.wireOp",EDGE,"E37")])],"isStart":false})]});
            var Q1;
            Q1=makeQuery(id+"F23.boolean.opBoolean","INTERSECT",EDGE,{"derivedFrom":[makeQuery(id+"F19.opExtrude","CAP_FACE",FACE,{"disambiguationData":[OSD([sQuery(id+"F18.wireOp",EDGE,"E26"),sQuery(id+"F18.wireOp",EDGE,"E27"),sQuery(id+"F18.wireOp",EDGE,"E28.bottom"),sQuery(id+"F18.wireOp",EDGE,"E28.left"),sQuery(id+"F18.wireOp",EDGE,"E29.bottom"),sQuery(id+"F18.wireOp",EDGE,"E29.left"),sQuery(id+"F18.wireOp",EDGE,"E30"),sQuery(id+"F18.wireOp",EDGE,"E31"),sQuery(id+"F18.wireOp",EDGE,"E32"),sQuery(id+"F18.wireOp",EDGE,"E33")])],"isStart":true}),makeQuery(id+"F23.opExtrude","CAP_FACE",FACE,{"disambiguationData":[OSD([sQuery(id+"F20.wireOp",EDGE,"E35"),sQuery(id+"F20.wireOp",EDGE,"E36"),sQuery(id+"F20.wireOp",EDGE,"E37")])],"isStart":true})]});
            var Q2;
            Q2=makeQuery(id+"F23.boolean.opBoolean","INTERSECT",EDGE,{"derivedFrom":[makeQuery(id+"F19.opExtrude","CAP_FACE",FACE,{"disambiguationData":[OSD([sQuery(id+"F18.wireOp",EDGE,"E26"),sQuery(id+"F18.wireOp",EDGE,"E27"),sQuery(id+"F18.wireOp",EDGE,"E28.bottom"),sQuery(id+"F18.wireOp",EDGE,"E28.left"),sQuery(id+"F18.wireOp",EDGE,"E29.bottom"),sQuery(id+"F18.wireOp",EDGE,"E29.left"),sQuery(id+"F18.wireOp",EDGE,"E30"),sQuery(id+"F18.wireOp",EDGE,"E31"),sQuery(id+"F18.wireOp",EDGE,"E32"),sQuery(id+"F18.wireOp",EDGE,"E33")])],"isStart":true}),makeQuery(id+"F23.opExtrude","SWEPT_FACE",FACE,{"disambiguationData":[OSD([sQuery(id+"F20.wireOp",EDGE,"E36")])]})]});
            var Q3;
            Q3=makeQuery(id+"F21.boolean.opBoolean","INTERSECT",EDGE,{"derivedFrom":[makeQuery(id+"F19.opExtrude","CAP_FACE",FACE,{"disambiguationData":[OSD([sQuery(id+"F18.wireOp",EDGE,"E26"),sQuery(id+"F18.wireOp",EDGE,"E27"),sQuery(id+"F18.wireOp",EDGE,"E28.bottom"),sQuery(id+"F18.wireOp",EDGE,"E28.left"),sQuery(id+"F18.wireOp",EDGE,"E29.bottom"),sQuery(id+"F18.wireOp",EDGE,"E29.left"),sQuery(id+"F18.wireOp",EDGE,"E30"),sQuery(id+"F18.wireOp",EDGE,"E31"),sQuery(id+"F18.wireOp",EDGE,"E32"),sQuery(id+"F18.wireOp",EDGE,"E33")])],"isStart":true}),makeQuery(id+"F21.opExtrude","SWEPT_FACE",FACE,{"disambiguationData":[OSD([sQuery(id+"F20.wireOp",EDGE,"E36")])]})]});
            fillet(context, id + "F24", {"entities" : qUnion([Q0, Q1, Q2, Q3]), "radius" : 3 * mm, "tangentPropagation" : true, "allowEdgeOverflow" : false});
        }
        {
            var Q0;
            Q0=makeQuery(id+"F19.opExtrude","CAP_FACE",FACE,{"disambiguationData":[OSD([sQuery(id+"F18.wireOp",EDGE,"E26"),sQuery(id+"F18.wireOp",EDGE,"E27"),sQuery(id+"F18.wireOp",EDGE,"E28.bottom"),sQuery(id+"F18.wireOp",EDGE,"E28.left"),sQuery(id+"F18.wireOp",EDGE,"E29.bottom"),sQuery(id+"F18.wireOp",EDGE,"E29.left"),sQuery(id+"F18.wireOp",EDGE,"E30"),sQuery(id+"F18.wireOp",EDGE,"E31"),sQuery(id+"F18.wireOp",EDGE,"E32"),sQuery(id+"F18.wireOp",EDGE,"E33")])],"isStart":true});
            var sketch = newSketch(context, id + "F25", { "sketchPlane" : qUnion([Q0])});
            skCircle(sketch, "E38", {"center": v(-56.62, -1.72) * mm, "radius": 3 * mm});
            skSolve(sketch);
        }
        {
            var Q0;
            Q0=makeQuery(id+"F25.imprint","IMPRINT",FACE,{"disambiguationData":[TD([[makeQuery(id+"F25.imprint","IMPRINT",EDGE,{"derivedFrom":makeQuery(id+"F19.opExtrude","CAP_EDGE",EDGE,{"disambiguationData":[OSD([sQuery(id+"F18.wireOp",EDGE,"E26")])],"isStart":true})}),1.0]])]});
            extrude(context, id + "F26", {"entities" : qUnion([Q0]), "operationType" : NewBodyOperationType.ADD, "depth" : 1.25 * mm});
        }
        {
            var Q0;
            {var subQ3=sQuery(id+"F18.wireOp",EDGE,"E30");var subQ4=sQuery(id+"F25.wireOp",EDGE,"E38");Q0=makeQuery(id+"F26.boolean.opBoolean","SPLIT",EDGE,{"disambiguationData":[TD([makeQuery(id+"F19.opExtrude","SWEPT_FACE",FACE,{"disambiguationData":[OSD([subQ3])]})])],"derivedFrom":makeQuery(id+"F26.opExtrude","CAP_EDGE",EDGE,{"disambiguationData":[OSD([subQ4])],"isStart":true})});}
            var Q1;
            {var subQ0=sQuery(id+"F18.wireOp",EDGE,"E31");var subQ5=sQuery(id+"F25.wireOp",EDGE,"E38");Q1=makeQuery(id+"F26.boolean.opBoolean","SPLIT",EDGE,{"disambiguationData":[TD([makeQuery(id+"F19.opExtrude","SWEPT_FACE",FACE,{"disambiguationData":[OSD([subQ0])]})])],"derivedFrom":makeQuery(id+"F26.opExtrude","CAP_EDGE",EDGE,{"disambiguationData":[OSD([subQ5])],"isStart":true})});}
            fillet(context, id + "F27", {"entities" : qUnion([Q0, Q1]), "radius" : 1 * mm, "tangentPropagation" : true, "allowEdgeOverflow" : false});
        }
        {
            var Q0;
            Q0=makeQuery(id+"F19.opExtrude","SWEPT_EDGE",EDGE,{"disambiguationData":[OSD([sQuery(id+"F18.wireOp",EDGE,"E27"),sQuery(id+"F18.wireOp",EDGE,"E33")])]});
            var Q1;
            Q1=makeQuery(id+"F19.opExtrude","SWEPT_EDGE",EDGE,{"disambiguationData":[OSD([sQuery(id+"F18.wireOp",EDGE,"E27"),sQuery(id+"F18.wireOp",EDGE,"E32")])]});
            fillet(context, id + "F28", {"entities" : qUnion([Q0, Q1]), "radius" : 1 * mm, "tangentPropagation" : true, "allowEdgeOverflow" : false});
        }
        {
            var Q0;
            Q0=makeQuery(id+"F19.opExtrude","CAP_FACE",FACE,{"disambiguationData":[OSD([sQuery(id+"F18.wireOp",EDGE,"E26"),sQuery(id+"F18.wireOp",EDGE,"E27"),sQuery(id+"F18.wireOp",EDGE,"E28.bottom"),sQuery(id+"F18.wireOp",EDGE,"E28.left"),sQuery(id+"F18.wireOp",EDGE,"E29.bottom"),sQuery(id+"F18.wireOp",EDGE,"E29.left"),sQuery(id+"F18.wireOp",EDGE,"E30"),sQuery(id+"F18.wireOp",EDGE,"E31"),sQuery(id+"F18.wireOp",EDGE,"E32"),sQuery(id+"F18.wireOp",EDGE,"E33")])],"isStart":false});
            var sketch = newSketch(context, id + "F29", { "sketchPlane" : qUnion([Q0])});
            skLineSegment(sketch, "E39", {"start": v(-56.8, 7.46) * mm, "end": v(-52.73, 5.14) * mm, "construction": true});
            skLineSegment(sketch, "E40", {"start": v(-56.8, -4.02) * mm, "end": v(-52.73, -1.7) * mm, "construction": true});
            skLineSegment(sketch, "E41", {"start": v(-54.76, 6.3) * mm, "end": v(-55.26, 5.43) * mm, "construction": true});
            skLineSegment(sketch, "E42", {"start": v(-55.26, 5.43) * mm, "end": v(-53.77, 8.04) * mm});
            skArc(sketch, "E43.0.startCap", {"start": v(-54.6, 5.06) * mm, "mid": v(-55.63, 4.78) * mm, "end": v(-55.9, 5.8) * mm});
            skArc(sketch, "E43.0.endCap", {"start": v(-54.42, 8.41) * mm, "mid": v(-53.4, 8.7) * mm, "end": v(-53.12, 7.67) * mm});
            skLineSegment(sketch, "E43.0.left", {"start": v(-55.9, 5.8) * mm, "end": v(-54.42, 8.41) * mm});
            skLineSegment(sketch, "E43.0.right", {"start": v(-54.6, 5.06) * mm, "end": v(-53.12, 7.67) * mm});
            skLineSegment(sketch, "E44", {"start": v(-54.76, -2.86) * mm, "end": v(-55.26, -2) * mm, "construction": true});
            skLineSegment(sketch, "E45", {"start": v(-55.26, -2) * mm, "end": v(-53.77, -4.6) * mm});
            skArc(sketch, "E46.0.startCap", {"start": v(-55.9, -2.37) * mm, "mid": v(-55.63, -1.34) * mm, "end": v(-54.6, -1.62) * mm});
            skArc(sketch, "E46.0.endCap", {"start": v(-53.12, -4.23) * mm, "mid": v(-53.4, -5.25) * mm, "end": v(-54.42, -4.97) * mm});
            skLineSegment(sketch, "E46.0.left", {"start": v(-54.6, -1.62) * mm, "end": v(-53.12, -4.23) * mm});
            skLineSegment(sketch, "E46.0.right", {"start": v(-55.9, -2.37) * mm, "end": v(-54.42, -4.97) * mm});
            skSolve(sketch);
        }
        {
            var Q0;
            Q0=makeQuery(id+"F29.imprint","IMPRINT",FACE,{"disambiguationData":[TD([[makeQuery(id+"F29.imprint","IMPRINT",EDGE,{"derivedFrom":sQuery(id+"F29.wireOp",EDGE,"E43.0.startCap")}),-1.0]])]});
            var Q1;
            Q1=makeQuery(id+"F29.imprint","IMPRINT",FACE,{"disambiguationData":[TD([[makeQuery(id+"F29.imprint","IMPRINT",EDGE,{"derivedFrom":sQuery(id+"F29.wireOp",EDGE,"E46.0.startCap")}),-1.0]])]});
            extrude(context, id + "F30", {"entities" : qUnion([Q0, Q1]), "operationType" : NewBodyOperationType.REMOVE, "oppositeDirection" : true, "depth" : 25 * mm});
        }
        {
            var Q0;
            Q0=makeQuery(id+"F1.opExtrude","SWEPT_EDGE",EDGE,{"disambiguationData":[OSD([sQuery(id+"F0.wireOp",EDGE,"E1.top"),sQuery(id+"F0.wireOp",EDGE,"E1.right")])]});
            var Q1;
            Q1=makeQuery(id+"F1.opExtrude","SWEPT_EDGE",EDGE,{"disambiguationData":[OSD([sQuery(id+"F0.wireOp",EDGE,"E1.bottom"),sQuery(id+"F0.wireOp",EDGE,"E1.right")])]});
            var Q2;
            Q2=makeQuery(id+"F1.opExtrude","SWEPT_EDGE",EDGE,{"disambiguationData":[OSD([sQuery(id+"F0.wireOp",EDGE,"E1.bottom"),sQuery(id+"F0.wireOp",EDGE,"E1.left")])]});
            var Q3;
            Q3=makeQuery(id+"F1.opExtrude","SWEPT_EDGE",EDGE,{"disambiguationData":[OSD([sQuery(id+"F0.wireOp",EDGE,"E1.top"),sQuery(id+"F0.wireOp",EDGE,"E1.left")])]});
            fillet(context, id + "F31", {"entities" : qUnion([Q0, Q1, Q2, Q3]), "radius" : 1 * mm, "tangentPropagation" : true, "allowEdgeOverflow" : false});
        }
        {
            var Q0;
            Q0=makeQuery(id+"F4.opExtrude","CAP_FACE",FACE,{"disambiguationData":[OSD([sQuery(id+"F3.wireOp",EDGE,"E4"),sQuery(id+"F3.wireOp",EDGE,"E5")])],"isStart":false});
            var sketch = newSketch(context, id + "F32", { "sketchPlane" : qUnion([Q0])});
            skLineSegment(sketch, "E47", {"start": v(0, 3) * mm, "end": v(0, 0) * mm});
            skArc(sketch, "E48.0.startCap", {"start": v(-0.1, 3) * mm, "mid": v(0, 3.1) * mm, "end": v(0.1, 3) * mm});
            skArc(sketch, "E48.0.endCap", {"start": v(0.1, 0) * mm, "mid": v(0, -0.1) * mm, "end": v(-0.1, 0) * mm});
            skLineSegment(sketch, "E48.0.left", {"start": v(0.1, 3) * mm, "end": v(0.1, 0) * mm});
            skLineSegment(sketch, "E48.0.right", {"start": v(-0.1, 3) * mm, "end": v(-0.1, 0) * mm});
            skSolve(sketch);
        }
        {
            var Q0;
            {var subQ0=sQuery(id+"F32.wireOp",EDGE,"E47");var subQ1=makeQuery(id+"F4.opExtrude","CAP_EDGE",EDGE,{"disambiguationData":[OSD([sQuery(id+"F3.wireOp",EDGE,"E4")])],"isStart":false});var subQ2=makeQuery(id+"F32.imprint","INTERSECT",VERTEX,{"derivedFrom":[subQ1,subQ0]});Q0=makeQuery(id+"F32.imprint","IMPRINT",FACE,{"disambiguationData":[TD([[makeQuery(id+"F32.imprint","IMPRINT",EDGE,{"disambiguationData":[TD([[subQ2,1.0]])],"derivedFrom":subQ0}),-1.0]])]});}
            var Q1;
            {var subQ0=sQuery(id+"F32.wireOp",EDGE,"E47");var subQ1=makeQuery(id+"F4.opExtrude","CAP_EDGE",EDGE,{"disambiguationData":[OSD([sQuery(id+"F3.wireOp",EDGE,"E4")])],"isStart":false});var subQ2=makeQuery(id+"F32.imprint","INTERSECT",VERTEX,{"derivedFrom":[subQ1,subQ0]});Q1=makeQuery(id+"F32.imprint","IMPRINT",FACE,{"disambiguationData":[TD([[makeQuery(id+"F32.imprint","IMPRINT",EDGE,{"disambiguationData":[TD([[subQ2,1.0]])],"derivedFrom":subQ0}),1.0]])]});}
            extrude(context, id + "F33", {"entities" : qUnion([Q0, Q1]), "operationType" : NewBodyOperationType.ADD, "depth" : 0.2 * mm});
        }
        {
            var Q0;
            Q0=makeQuery(id+"F6.opExtrude","CAP_FACE",FACE,{"disambiguationData":[OSD([sQuery(id+"F5.wireOp",EDGE,"E7"),sQuery(id+"F5.wireOp",EDGE,"E8")])],"isStart":false});
            var sketch = newSketch(context, id + "F34", { "sketchPlane" : qUnion([Q0])});
            skLineSegment(sketch, "E49", {"start": v(0, 3) * mm, "end": v(0, 0) * mm});
            skArc(sketch, "E50.0.startCap", {"start": v(-0.1, 3) * mm, "mid": v(0, 3.1) * mm, "end": v(0.1, 3) * mm});
            skArc(sketch, "E50.0.endCap", {"start": v(0.1, 0) * mm, "mid": v(0, -0.1) * mm, "end": v(-0.1, 0) * mm});
            skLineSegment(sketch, "E50.0.left", {"start": v(0.1, 3) * mm, "end": v(0.1, 0) * mm});
            skLineSegment(sketch, "E50.0.right", {"start": v(-0.1, 3) * mm, "end": v(-0.1, 0) * mm});
            skSolve(sketch);
        }
        {
            var Q0;
            {var subQ0=sQuery(id+"F34.wireOp",EDGE,"E49");var subQ1=makeQuery(id+"F6.opExtrude","CAP_EDGE",EDGE,{"disambiguationData":[OSD([sQuery(id+"F5.wireOp",EDGE,"E7")])],"isStart":false});var subQ2=makeQuery(id+"F34.imprint","INTERSECT",VERTEX,{"derivedFrom":[subQ1,subQ0]});Q0=makeQuery(id+"F34.imprint","IMPRINT",FACE,{"disambiguationData":[TD([[makeQuery(id+"F34.imprint","IMPRINT",EDGE,{"disambiguationData":[TD([[subQ2,1.0]])],"derivedFrom":subQ0}),-1.0]])]});}
            var Q1;
            {var subQ0=sQuery(id+"F34.wireOp",EDGE,"E49");var subQ1=makeQuery(id+"F6.opExtrude","CAP_EDGE",EDGE,{"disambiguationData":[OSD([sQuery(id+"F5.wireOp",EDGE,"E7")])],"isStart":false});var subQ2=makeQuery(id+"F34.imprint","INTERSECT",VERTEX,{"derivedFrom":[subQ1,subQ0]});Q1=makeQuery(id+"F34.imprint","IMPRINT",FACE,{"disambiguationData":[TD([[makeQuery(id+"F34.imprint","IMPRINT",EDGE,{"disambiguationData":[TD([[subQ2,1.0]])],"derivedFrom":subQ0}),1.0]])]});}
            extrude(context, id + "F35", {"entities" : qUnion([Q0, Q1]), "operationType" : NewBodyOperationType.ADD, "depth" : 0.2 * mm});
        }
        {
            var Q0;
            Q0=makeQuery(id+"F19.opExtrude","CAP_FACE",FACE,{"disambiguationData":[OSD([sQuery(id+"F18.wireOp",EDGE,"E26"),sQuery(id+"F18.wireOp",EDGE,"E27"),sQuery(id+"F18.wireOp",EDGE,"E28.bottom"),sQuery(id+"F18.wireOp",EDGE,"E28.left"),sQuery(id+"F18.wireOp",EDGE,"E29.bottom"),sQuery(id+"F18.wireOp",EDGE,"E29.left"),sQuery(id+"F18.wireOp",EDGE,"E30"),sQuery(id+"F18.wireOp",EDGE,"E31"),sQuery(id+"F18.wireOp",EDGE,"E32"),sQuery(id+"F18.wireOp",EDGE,"E33")])],"isStart":false});
            var sketch = newSketch(context, id + "F36", { "sketchPlane" : qUnion([Q0])});
            skLineSegment(sketch, "E51", {"start": v(-56.62, 1.72) * mm, "end": v(-53.62, 1.72) * mm, "construction": true});
            skLineSegment(sketch, "E52.1.0", {"start": v(-56.62, 1.72) * mm, "end": v(-53.66, 2.24) * mm, "construction": true});
            skLineSegment(sketch, "E52.2.0", {"start": v(-56.62, 1.72) * mm, "end": v(-53.8, 2.75) * mm, "construction": true});
            skLineSegment(sketch, "E52.3.0", {"start": v(-56.62, 1.72) * mm, "end": v(-54.02, 3.22) * mm, "construction": true});
            skLineSegment(sketch, "E52.4.0", {"start": v(-56.62, 1.72) * mm, "end": v(-54.32, 3.65) * mm, "construction": true});
            skLineSegment(sketch, "E52.5.0", {"start": v(-56.62, 1.72) * mm, "end": v(-54.69, 4.02) * mm, "construction": true});
            skLineSegment(sketch, "E52.6.0", {"start": v(-56.62, 1.72) * mm, "end": v(-55.12, 4.32) * mm, "construction": true});
            skLineSegment(sketch, "E52.7.0", {"start": v(-56.62, 1.72) * mm, "end": v(-55.6, 4.54) * mm, "construction": true});
            skLineSegment(sketch, "E52.8.0", {"start": v(-56.62, 1.72) * mm, "end": v(-56.1, 4.67) * mm, "construction": true});
            skLineSegment(sketch, "E52.9.0", {"start": v(-56.62, 1.72) * mm, "end": v(-56.62, 4.72) * mm, "construction": true});
            skLineSegment(sketch, "E52.10.0", {"start": v(-56.62, 1.72) * mm, "end": v(-57.14, 4.67) * mm, "construction": true});
            skLineSegment(sketch, "E52.11.0", {"start": v(-56.62, 1.72) * mm, "end": v(-57.64, 4.54) * mm, "construction": true});
            skLineSegment(sketch, "E52.12.0", {"start": v(-56.62, 1.72) * mm, "end": v(-58.12, 4.32) * mm, "construction": true});
            skLineSegment(sketch, "E52.13.0", {"start": v(-56.62, 1.72) * mm, "end": v(-58.54, 4.02) * mm, "construction": true});
            skLineSegment(sketch, "E52.14.0", {"start": v(-56.62, 1.72) * mm, "end": v(-58.91, 3.65) * mm, "construction": true});
            skLineSegment(sketch, "E52.15.0", {"start": v(-56.62, 1.72) * mm, "end": v(-59.21, 3.22) * mm, "construction": true});
            skLineSegment(sketch, "E52.16.0", {"start": v(-56.62, 1.72) * mm, "end": v(-59.44, 2.75) * mm, "construction": true});
            skLineSegment(sketch, "E52.17.0", {"start": v(-56.62, 1.72) * mm, "end": v(-59.57, 2.24) * mm, "construction": true});
            skLineSegment(sketch, "E52.18.0", {"start": v(-56.62, 1.72) * mm, "end": v(-59.62, 1.72) * mm, "construction": true});
            skLineSegment(sketch, "E52.19.0", {"start": v(-56.62, 1.72) * mm, "end": v(-59.57, 1.2) * mm, "construction": true});
            skLineSegment(sketch, "E52.20.0", {"start": v(-56.62, 1.72) * mm, "end": v(-59.44, 0.7) * mm, "construction": true});
            skLineSegment(sketch, "E52.21.0", {"start": v(-56.62, 1.72) * mm, "end": v(-59.21, 0.22) * mm, "construction": true});
            skLineSegment(sketch, "E52.22.0", {"start": v(-56.62, 1.72) * mm, "end": v(-58.91, -0.2) * mm, "construction": true});
            skLineSegment(sketch, "E52.23.0", {"start": v(-56.62, 1.72) * mm, "end": v(-58.54, -0.58) * mm, "construction": true});
            skLineSegment(sketch, "E52.24.0", {"start": v(-56.62, 1.72) * mm, "end": v(-58.12, -0.88) * mm, "construction": true});
            skLineSegment(sketch, "E52.25.0", {"start": v(-56.62, 1.72) * mm, "end": v(-57.64, -1.1) * mm, "construction": true});
            skLineSegment(sketch, "E52.26.0", {"start": v(-56.62, 1.72) * mm, "end": v(-57.14, -1.24) * mm, "construction": true});
            skLineSegment(sketch, "E52.27.0", {"start": v(-56.62, 1.72) * mm, "end": v(-56.62, -1.28) * mm, "construction": true});
            skLineSegment(sketch, "E52.28.0", {"start": v(-56.62, 1.72) * mm, "end": v(-56.1, -1.24) * mm, "construction": true});
            skLineSegment(sketch, "E52.29.0", {"start": v(-56.62, 1.72) * mm, "end": v(-55.6, -1.1) * mm, "construction": true});
            skLineSegment(sketch, "E52.30.0", {"start": v(-56.62, 1.72) * mm, "end": v(-55.12, -0.88) * mm, "construction": true});
            skLineSegment(sketch, "E52.31.0", {"start": v(-56.62, 1.72) * mm, "end": v(-54.69, -0.58) * mm, "construction": true});
            skLineSegment(sketch, "E52.32.0", {"start": v(-56.62, 1.72) * mm, "end": v(-54.32, -0.2) * mm, "construction": true});
            skLineSegment(sketch, "E52.33.0", {"start": v(-56.62, 1.72) * mm, "end": v(-54.02, 0.22) * mm, "construction": true});
            skLineSegment(sketch, "E52.34.0", {"start": v(-56.62, 1.72) * mm, "end": v(-53.8, 0.7) * mm, "construction": true});
            skLineSegment(sketch, "E52.35.0", {"start": v(-56.62, 1.72) * mm, "end": v(-53.66, 1.2) * mm, "construction": true});
            skPoint(sketch, "E52.center", {"position": v(-56.62, 1.72) * mm});
            skArc(sketch, "E53.0.startCap", {"start": v(-56.62, 1.54) * mm, "mid": v(-56.8, 1.72) * mm, "end": v(-56.62, 1.9) * mm});
            skArc(sketch, "E53.0.endCap", {"start": v(-53.62, 1.9) * mm, "mid": v(-53.44, 1.72) * mm, "end": v(-53.62, 1.54) * mm});
            skLineSegment(sketch, "E53.0.left", {"start": v(-56.62, 1.9) * mm, "end": v(-53.62, 1.9) * mm});
            skLineSegment(sketch, "E53.0.right", {"start": v(-56.62, 1.54) * mm, "end": v(-53.62, 1.54) * mm});
            skArc(sketch, "E54.0.startCap", {"start": v(-56.59, 1.55) * mm, "mid": v(-56.79, 1.69) * mm, "end": v(-56.65, 1.9) * mm});
            skArc(sketch, "E54.0.endCap", {"start": v(-53.7, 2.41) * mm, "mid": v(-53.49, 2.27) * mm, "end": v(-53.63, 2.07) * mm});
            skLineSegment(sketch, "E54.0.left", {"start": v(-56.65, 1.9) * mm, "end": v(-53.7, 2.41) * mm});
            skLineSegment(sketch, "E54.0.right", {"start": v(-56.59, 1.55) * mm, "end": v(-53.63, 2.07) * mm});
            skArc(sketch, "E55.0.startCap", {"start": v(-56.56, 1.55) * mm, "mid": v(-56.78, 1.66) * mm, "end": v(-56.68, 1.88) * mm});
            skArc(sketch, "E55.0.endCap", {"start": v(-53.86, 2.9) * mm, "mid": v(-53.63, 2.8) * mm, "end": v(-53.74, 2.58) * mm});
            skLineSegment(sketch, "E55.0.left", {"start": v(-56.68, 1.88) * mm, "end": v(-53.86, 2.9) * mm});
            skLineSegment(sketch, "E55.0.right", {"start": v(-56.56, 1.55) * mm, "end": v(-53.74, 2.58) * mm});
            skArc(sketch, "E55.1.startCap", {"start": v(-56.53, 1.57) * mm, "mid": v(-56.77, 1.63) * mm, "end": v(-56.7, 1.87) * mm});
            skArc(sketch, "E55.1.endCap", {"start": v(-54.1, 3.37) * mm, "mid": v(-53.87, 3.3) * mm, "end": v(-53.93, 3.07) * mm});
            skLineSegment(sketch, "E55.1.left", {"start": v(-56.7, 1.87) * mm, "end": v(-54.1, 3.37) * mm});
            skLineSegment(sketch, "E55.1.right", {"start": v(-56.53, 1.57) * mm, "end": v(-53.93, 3.07) * mm});
            skArc(sketch, "E55.2.startCap", {"start": v(-56.5, 1.59) * mm, "mid": v(-56.75, 1.6) * mm, "end": v(-56.73, 1.85) * mm});
            skArc(sketch, "E55.2.endCap", {"start": v(-54.43, 3.78) * mm, "mid": v(-54.18, 3.76) * mm, "end": v(-54.2, 3.51) * mm});
            skLineSegment(sketch, "E55.2.left", {"start": v(-56.73, 1.85) * mm, "end": v(-54.43, 3.78) * mm});
            skLineSegment(sketch, "E55.2.right", {"start": v(-56.5, 1.59) * mm, "end": v(-54.2, 3.51) * mm});
            skArc(sketch, "E55.3.startCap", {"start": v(-56.48, 1.6) * mm, "mid": v(-56.73, 1.59) * mm, "end": v(-56.75, 1.83) * mm});
            skArc(sketch, "E55.3.endCap", {"start": v(-54.82, 4.13) * mm, "mid": v(-54.58, 4.15) * mm, "end": v(-54.55, 3.9) * mm});
            skLineSegment(sketch, "E55.3.left", {"start": v(-56.75, 1.83) * mm, "end": v(-54.82, 4.13) * mm});
            skLineSegment(sketch, "E55.3.right", {"start": v(-56.48, 1.6) * mm, "end": v(-54.55, 3.9) * mm});
            skArc(sketch, "E55.4.startCap", {"start": v(-56.65, 1.55) * mm, "mid": v(-56.79, 1.75) * mm, "end": v(-56.59, 1.9) * mm});
            skArc(sketch, "E55.4.endCap", {"start": v(-53.63, 1.37) * mm, "mid": v(-53.49, 1.17) * mm, "end": v(-53.7, 1.03) * mm});
            skLineSegment(sketch, "E55.4.left", {"start": v(-56.59, 1.9) * mm, "end": v(-53.63, 1.37) * mm});
            skLineSegment(sketch, "E55.4.right", {"start": v(-56.65, 1.55) * mm, "end": v(-53.7, 1.03) * mm});
            skArc(sketch, "E55.5.startCap", {"start": v(-56.68, 1.55) * mm, "mid": v(-56.78, 1.78) * mm, "end": v(-56.56, 1.88) * mm});
            skArc(sketch, "E55.5.endCap", {"start": v(-53.74, 0.86) * mm, "mid": v(-53.63, 0.63) * mm, "end": v(-53.86, 0.53) * mm});
            skLineSegment(sketch, "E55.5.left", {"start": v(-56.56, 1.88) * mm, "end": v(-53.74, 0.86) * mm});
            skLineSegment(sketch, "E55.5.right", {"start": v(-56.68, 1.55) * mm, "end": v(-53.86, 0.53) * mm});
            skArc(sketch, "E55.6.startCap", {"start": v(-56.7, 1.57) * mm, "mid": v(-56.77, 1.8) * mm, "end": v(-56.53, 1.87) * mm});
            skArc(sketch, "E55.6.endCap", {"start": v(-53.93, 0.37) * mm, "mid": v(-53.87, 0.13) * mm, "end": v(-54.1, 0.07) * mm});
            skLineSegment(sketch, "E55.6.left", {"start": v(-56.53, 1.87) * mm, "end": v(-53.93, 0.37) * mm});
            skLineSegment(sketch, "E55.6.right", {"start": v(-56.7, 1.57) * mm, "end": v(-54.1, 0.07) * mm});
            skArc(sketch, "E55.7.startCap", {"start": v(-56.73, 1.59) * mm, "mid": v(-56.75, 1.83) * mm, "end": v(-56.5, 1.85) * mm});
            skArc(sketch, "E55.7.endCap", {"start": v(-54.2, -0.08) * mm, "mid": v(-54.18, -0.32) * mm, "end": v(-54.43, -0.34) * mm});
            skLineSegment(sketch, "E55.7.left", {"start": v(-56.5, 1.85) * mm, "end": v(-54.2, -0.08) * mm});
            skLineSegment(sketch, "E55.7.right", {"start": v(-56.73, 1.59) * mm, "end": v(-54.43, -0.34) * mm});
            skArc(sketch, "E55.8.startCap", {"start": v(-56.75, 1.6) * mm, "mid": v(-56.73, 1.85) * mm, "end": v(-56.48, 1.83) * mm});
            skArc(sketch, "E55.8.endCap", {"start": v(-54.55, -0.47) * mm, "mid": v(-54.58, -0.71) * mm, "end": v(-54.82, -0.7) * mm});
            skLineSegment(sketch, "E55.8.left", {"start": v(-56.48, 1.83) * mm, "end": v(-54.55, -0.47) * mm});
            skLineSegment(sketch, "E55.8.right", {"start": v(-56.75, 1.6) * mm, "end": v(-54.82, -0.7) * mm});
            skSolve(sketch);
        }
        {
            var Q0;
            Q0 = qSketchRegion(id + "F36", true);
            extrude(context, id + "F37", {"entities" : qUnion([Q0]), "operationType" : NewBodyOperationType.REMOVE, "oppositeDirection" : true, "depth" : 0.3 * mm});
        }
    });
